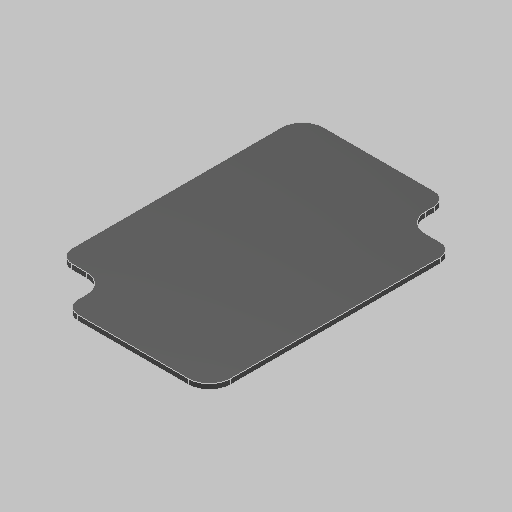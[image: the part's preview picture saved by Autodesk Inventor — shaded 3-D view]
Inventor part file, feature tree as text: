
AUTODESK INVENTOR PART (.ipt)
format: ipt  version: 2023.5 (Build 275446000, 446)  size: 94,720 bytes
history: native  units: in
note: dims shown in document units (in); Inventor stores cm internally (conversion verified against a paired STEP export)
features: fillet x1
ambient origin geometry x8: Origin, YZ Plane, XZ Plane, XY Plane, X Axis, Y Axis, Z Axis, Center Point
bodies: Solid1 (feature_tree)
feature tree (1):
  fillet  "Fillet3"  [1 undecoded]
note: 1 required parameter value undecoded (feature->parameter linkage not recoverable at this tier; creation-order binding heuristic only, values carry confidence <= 0.55)
